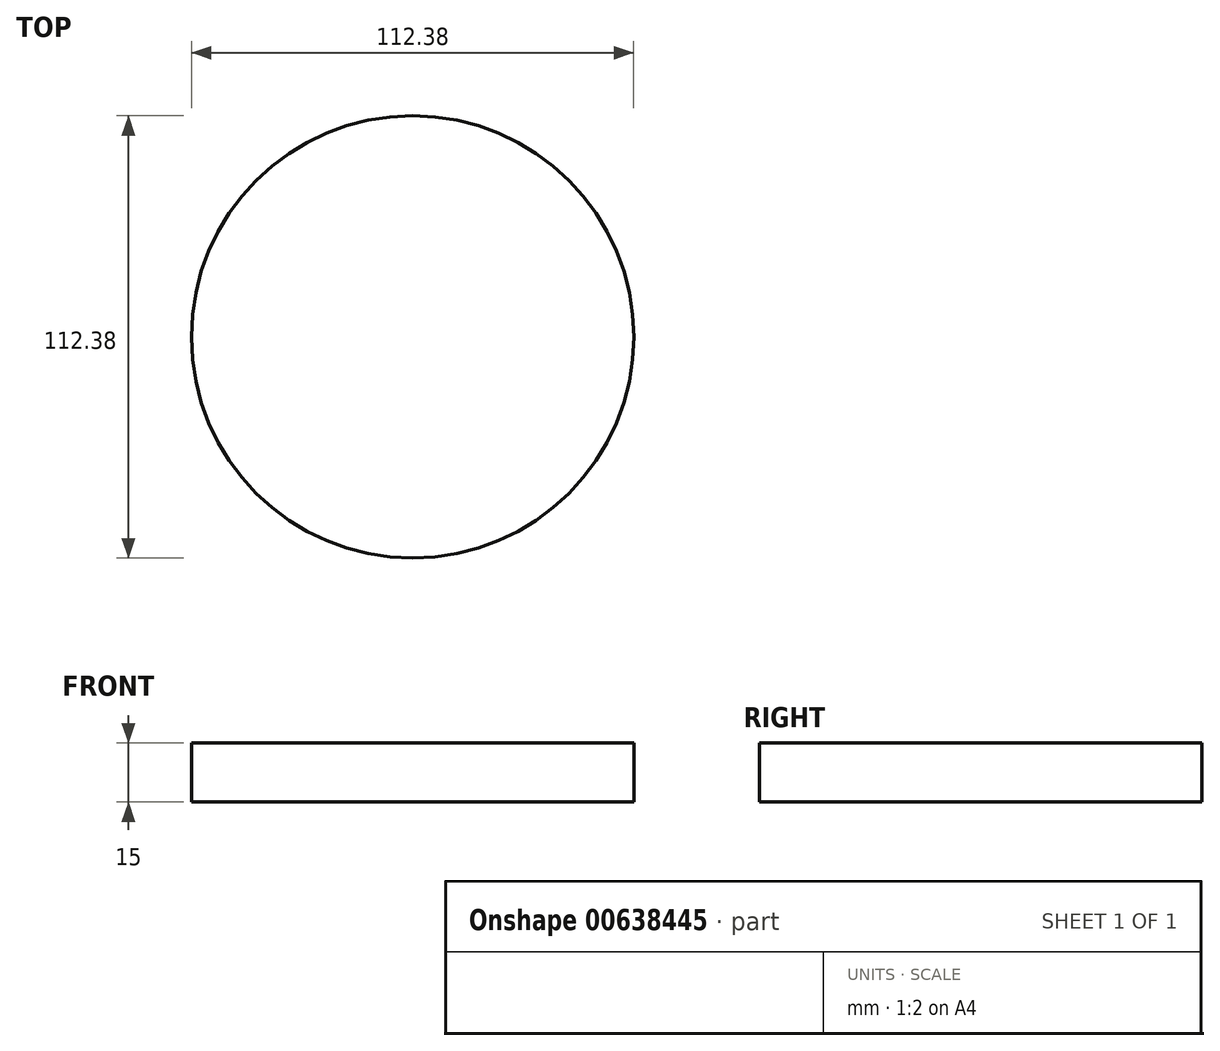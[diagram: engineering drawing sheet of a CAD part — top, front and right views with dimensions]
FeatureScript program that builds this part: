
annotation { "Feature Type Name" : "Feature", "Feature Type Description" : "" }
export const myFeature = defineFeature(function(context is Context, id is Id, definition is map)
    precondition{}
    {
        {
            var Q0;
            Q0=qCreatedBy(makeId("Top.planeOp"),FACE);
            var sketch = newSketch(context, id + "F0", { "sketchPlane" : qUnion([Q0])});
            skCircle(sketch, "E0", {"center": v(0, 0) * mm, "radius": 56.2 * mm});
            skSolve(sketch);
        }
        {
            var Q0;
            Q0 = qSketchRegion(id + "F0", true);
            extrude(context, id + "F1", {"entities" : qUnion([Q0]), "depth" : 15 * mm, "offsetDistance" : 25 * mm});
        }
    });
